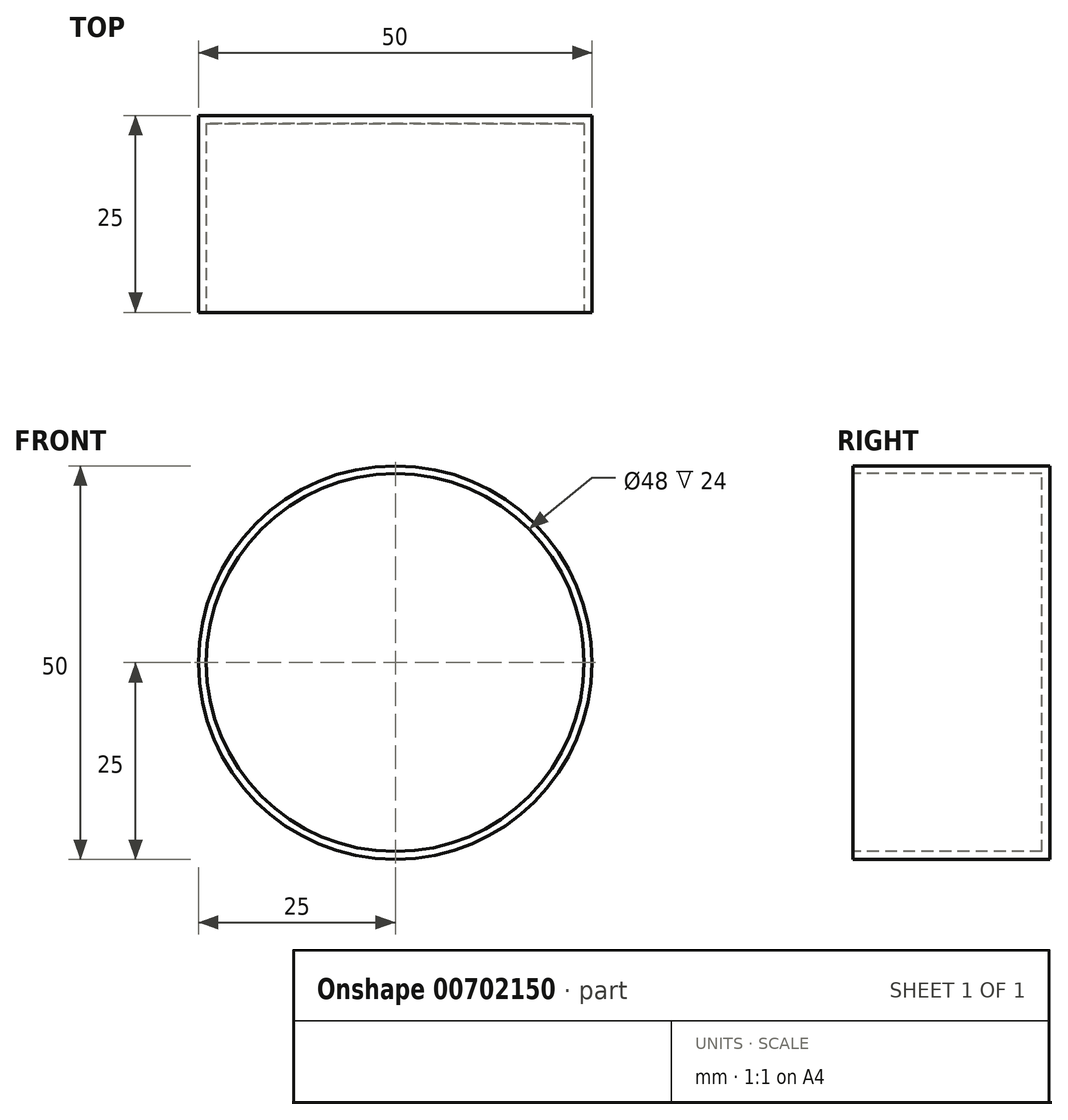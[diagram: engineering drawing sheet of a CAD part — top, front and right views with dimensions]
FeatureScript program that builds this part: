
annotation { "Feature Type Name" : "Feature", "Feature Type Description" : "" }
export const myFeature = defineFeature(function(context is Context, id is Id, definition is map)
    precondition{}
    {
        {
            var Q0;
            Q0=qCreatedBy(makeId("Front.planeOp"),FACE);
            var sketch = newSketch(context, id + "F0", { "sketchPlane" : qUnion([Q0])});
            skCircle(sketch, "E0", {"center": v(0, 0) * mm, "radius": 25 * mm});
            skSolve(sketch);
        }
        {
            var Q0;
            Q0=makeQuery(id+"F0.imprint","IMPRINT",FACE,{"disambiguationData":[TD([[makeQuery(id+"F0.imprint","IMPRINT",EDGE,{"derivedFrom":sQuery(id+"F0.wireOp",EDGE,"E0")}),1.0]])]});
            extrude(context, id + "F1", {"entities" : qUnion([Q0]), "depth" : 25 * mm, "offsetDistance" : 25 * mm});
        }
        {
            var Q0;
            Q0=makeQuery(id+"F1.opExtrude","CAP_FACE",FACE,{"disambiguationData":[OSD([sQuery(id+"F0.wireOp",EDGE,"E0")])],"isStart":false});
            var sketch = newSketch(context, id + "F2", { "sketchPlane" : qUnion([Q0])});
            skCircle(sketch, "E1", {"center": v(0, 0) * mm, "radius": 24 * mm});
            skSolve(sketch);
        }
        {
            var Q0;
            Q0=makeQuery(id+"F2.imprint","IMPRINT",FACE,{"disambiguationData":[TD([[makeQuery(id+"F2.imprint","IMPRINT",EDGE,{"derivedFrom":sQuery(id+"F2.wireOp",EDGE,"E1")}),1.0]])]});
            var Q1;
            Q1=sQuery(id+"F2.wireOp",EDGE,"E1");
            extrude(context, id + "F3", {"entities" : qUnion([Q0]), "operationType" : NewBodyOperationType.REMOVE, "surfaceEntities" : qUnion([Q1]), "oppositeDirection" : true, "depth" : 24 * mm, "offsetDistance" : 25 * mm});
        }
    });
